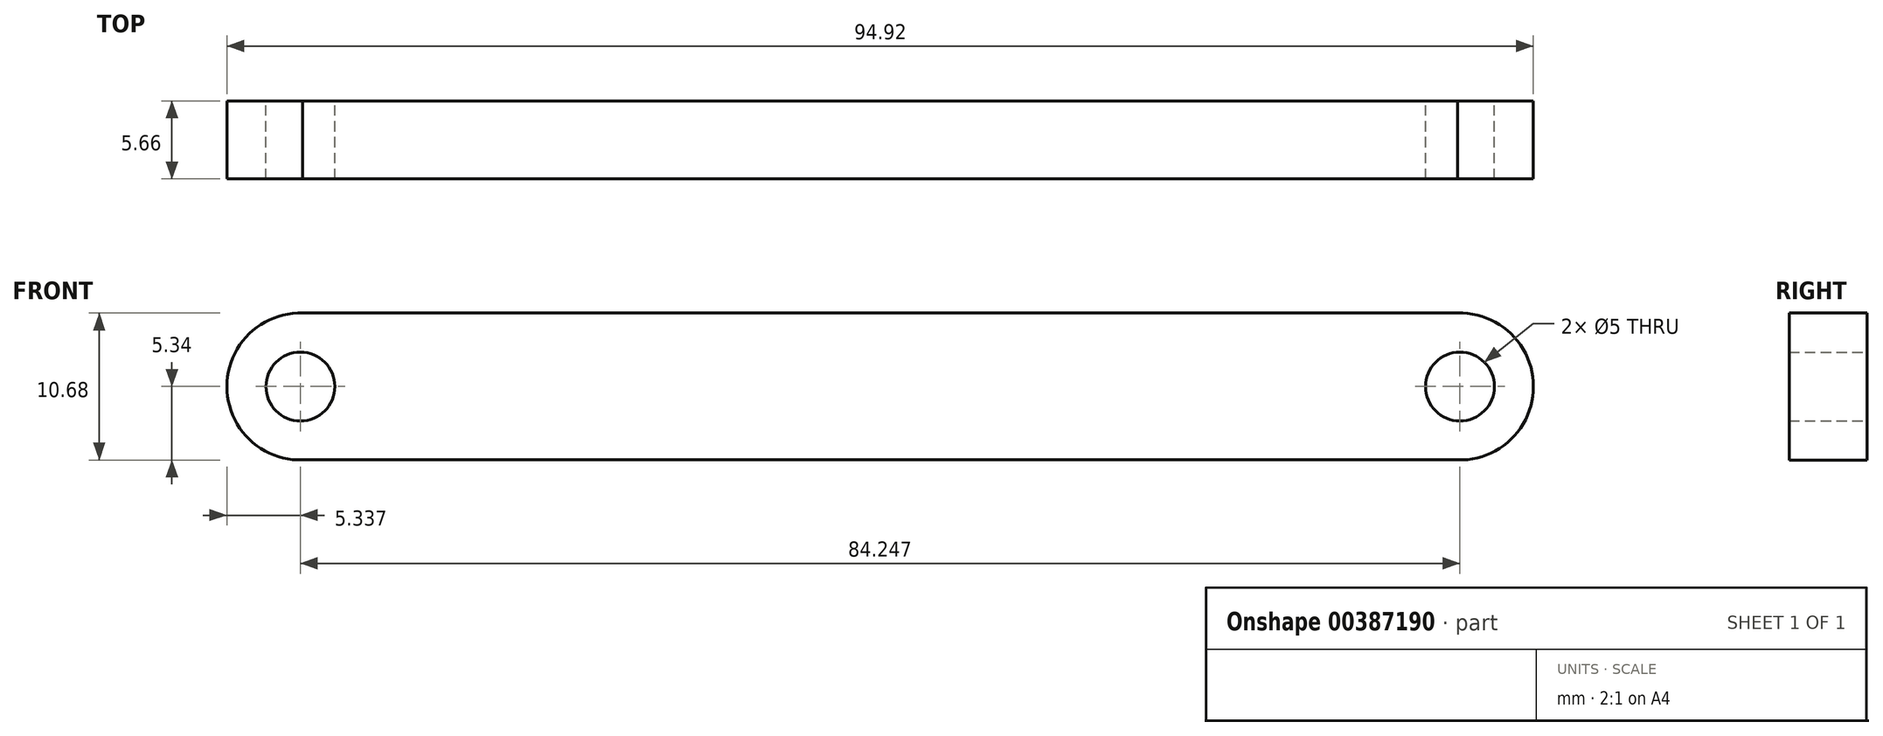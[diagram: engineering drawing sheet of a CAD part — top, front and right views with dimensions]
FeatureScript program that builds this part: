
annotation { "Feature Type Name" : "Feature", "Feature Type Description" : "" }
export const myFeature = defineFeature(function(context is Context, id is Id, definition is map)
    precondition{}
    {
        {
            var Q0;
            Q0=qCreatedBy(makeId("Front.planeOp"),FACE);
            var sketch = newSketch(context, id + "F0", { "sketchPlane" : qUnion([Q0])});
            skLineSegment(sketch, "E0.bottom", {"start": v(42.3, -5.33) * mm, "end": v(-42.3, -5.33) * mm});
            skLineSegment(sketch, "E0.top", {"start": v(42.3, 5.33) * mm, "end": v(-42.3, 5.33) * mm});
            skPoint(sketch, "E0.middle", {"position": v(0, 0) * mm});
            skCircle(sketch, "E1", {"center": v(-42.12, 0) * mm, "radius": 2.5 * mm});
            skCircle(sketch, "E2.MirrorC", {"center": v(42.12, 0) * mm, "radius": 2.5 * mm});
            skArc(sketch, "E3", {"start": v(-41.96, 5.33) * mm, "mid": v(-47.46, 0) * mm, "end": v(-41.96, -5.33) * mm});
            skArc(sketch, "E4.MirrorC", {"start": v(41.96, 5.33) * mm, "mid": v(47.46, 0) * mm, "end": v(41.96, -5.33) * mm});
            skSolve(sketch);
        }
        {
            var Q0;
            Q0 = qSketchRegion(id + "F0", true);
            extrude(context, id + "F1", {"entities" : qUnion([Q0]), "depth" : 5.66 * mm});
        }
    });
